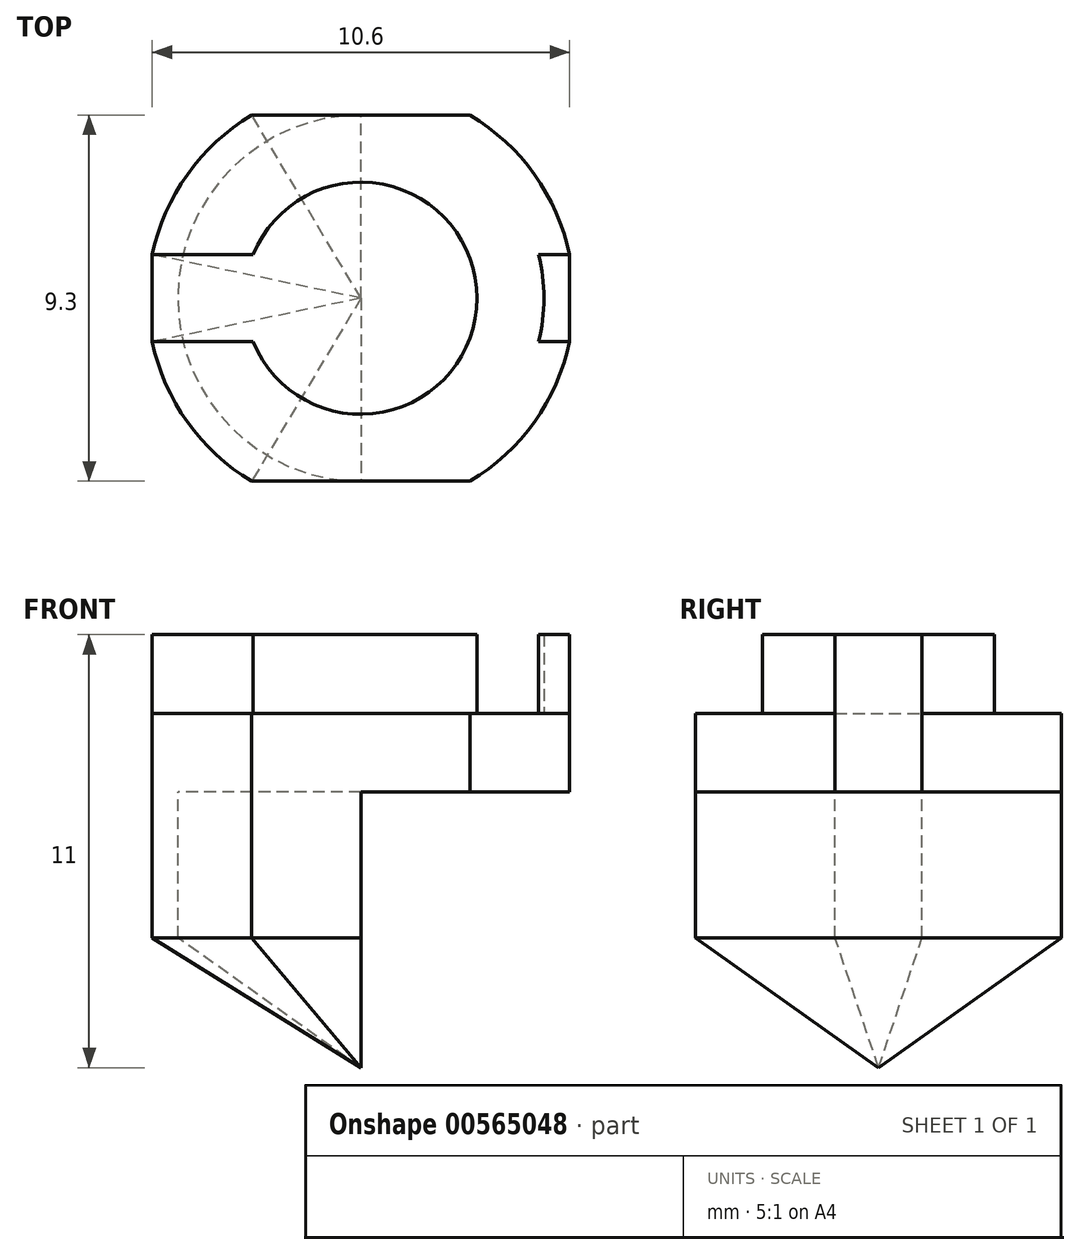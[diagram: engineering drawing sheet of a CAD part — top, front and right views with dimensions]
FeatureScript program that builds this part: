
annotation { "Feature Type Name" : "Feature", "Feature Type Description" : "" }
export const myFeature = defineFeature(function(context is Context, id is Id, definition is map)
    precondition{}
    {
        {
            var Q0;
            Q0=qCreatedBy(makeId("Top.planeOp"),FACE);
            var sketch = newSketch(context, id + "F0", { "sketchPlane" : qUnion([Q0])});
            skLineSegment(sketch, "E0.top", {"start": v(-2.77, 4.65) * mm, "end": v(0, 4.65) * mm});
            skArc(sketch, "E1", {"start": v(0, 2.95) * mm, "mid": v(-2.09, 2.09) * mm, "end": v(-2.95, 0) * mm});
            skLineSegment(sketch, "E2.bottom", {"start": v(-5.3, 1.1) * mm, "end": v(-2.74, 1.1) * mm});
            skPoint(sketch, "E2.middle", {"position": v(-2.95, 0) * mm});
            skArc(sketch, "E3", {"start": v(0, 4.65) * mm, "mid": v(-2.87, 3.66) * mm, "end": v(-4.52, 1.1) * mm});
            skArc(sketch, "E4.0", {"start": v(-2.77, 4.65) * mm, "mid": v(-4.4, 3.14) * mm, "end": v(-5.3, 1.1) * mm});
            skPoint(sketch, "E5", {"position": v(0, 2.95) * mm});
            skLineSegment(sketch, "E6.MirrorCS", {"start": v(2.77, 4.65) * mm, "end": v(0, 4.65) * mm});
            skArc(sketch, "E7.MirrorCS", {"start": v(0, 4.65) * mm, "mid": v(2.87, 3.66) * mm, "end": v(4.52, 1.1) * mm});
            skArc(sketch, "E8.MirrorCS", {"start": v(2.77, 4.65) * mm, "mid": v(4.4, 3.14) * mm, "end": v(5.3, 1.1) * mm});
            skArc(sketch, "E9.MirrorCS", {"start": v(0, 2.95) * mm, "mid": v(2.09, 2.09) * mm, "end": v(2.95, 0) * mm});
            skLineSegment(sketch, "E10.MirrorCS", {"start": v(5.3, 1.1) * mm, "end": v(2.74, 1.1) * mm});
            skArc(sketch, "E11.MirrorCS", {"start": v(0, -2.95) * mm, "mid": v(-2.09, -2.09) * mm, "end": v(-2.95, 0) * mm});
            skArc(sketch, "E12.MirrorCS", {"start": v(0, -2.95) * mm, "mid": v(2.09, -2.09) * mm, "end": v(2.95, 0) * mm});
            skLineSegment(sketch, "E13.MirrorCS", {"start": v(5.3, -1.1) * mm, "end": v(2.74, -1.1) * mm});
            skLineSegment(sketch, "E14.MirrorCS", {"start": v(-5.3, -1.1) * mm, "end": v(-2.74, -1.1) * mm});
            skArc(sketch, "E15.MirrorCS", {"start": v(0, -4.65) * mm, "mid": v(-2.87, -3.66) * mm, "end": v(-4.52, -1.1) * mm});
            skArc(sketch, "E16.MirrorCS", {"start": v(-2.77, -4.65) * mm, "mid": v(-4.4, -3.14) * mm, "end": v(-5.3, -1.1) * mm});
            skLineSegment(sketch, "E17.MirrorCS", {"start": v(-2.77, -4.65) * mm, "end": v(0, -4.65) * mm});
            skLineSegment(sketch, "E18.MirrorCS", {"start": v(2.77, -4.65) * mm, "end": v(0, -4.65) * mm});
            skArc(sketch, "E19.MirrorCS", {"start": v(2.77, -4.65) * mm, "mid": v(4.4, -3.14) * mm, "end": v(5.3, -1.1) * mm});
            skArc(sketch, "E20.MirrorCS", {"start": v(0, -4.65) * mm, "mid": v(2.87, -3.66) * mm, "end": v(4.52, -1.1) * mm});
            skLineSegment(sketch, "E21", {"start": v(-5.3, 1.1) * mm, "end": v(-5.3, -1.1) * mm});
            skLineSegment(sketch, "E22", {"start": v(5.3, 1.1) * mm, "end": v(5.3, -1.1) * mm});
            skCircle(sketch, "E23", {"center": v(0, 0) * mm, "radius": 4.65 * mm});
            skSolve(sketch);
        }
        {
            var Q0;
            {var subQ8=sQuery(id+"F0.wireOp",EDGE,"E21");Q0=makeQuery(id+"F0.imprint","IMPRINT",FACE,{"disambiguationData":[TD([[makeQuery(id+"F0.imprint","IMPRINT",EDGE,{"derivedFrom":subQ8}),1.0]])]});}
            var Q1;
            {var subQ0=sQuery(id+"F0.wireOp",EDGE,"E9.MirrorCS");var subQ1=sQuery(id+"F0.wireOp",EDGE,"E1");var subQ2=makeQuery(id+"F0.imprint","INTERSECT",VERTEX,{"derivedFrom":[subQ1,subQ0]});Q1=makeQuery(id+"F0.imprint","IMPRINT",FACE,{"disambiguationData":[TD([[makeQuery(id+"F0.imprint","IMPRINT",EDGE,{"disambiguationData":[TD([[subQ2,-1.0]])],"derivedFrom":subQ1}),1.0]])]});}
            var Q2;
            {var subQ8=sQuery(id+"F0.wireOp",EDGE,"E22");Q2=makeQuery(id+"F0.imprint","IMPRINT",FACE,{"disambiguationData":[TD([[makeQuery(id+"F0.imprint","IMPRINT",EDGE,{"derivedFrom":subQ8}),-1.0]])]});}
            var Q3;
            {var subQ0=sQuery(id+"F0.wireOp",EDGE,"E11.MirrorCS");var subQ1=sQuery(id+"F0.wireOp",EDGE,"E1");var subQ2=makeQuery(id+"F0.imprint","INTERSECT",VERTEX,{"derivedFrom":[subQ1,subQ0]});Q3=makeQuery(id+"F0.imprint","IMPRINT",FACE,{"disambiguationData":[TD([[makeQuery(id+"F0.imprint","IMPRINT",EDGE,{"disambiguationData":[TD([[subQ2,1.0]])],"derivedFrom":subQ1}),-1.0]])]});}
            var Q4;
            {var subQ1=sQuery(id+"F0.wireOp",EDGE,"E12.MirrorCS");var subQ5=sQuery(id+"F0.wireOp",EDGE,"E9.MirrorCS");var subQ6=makeQuery(id+"F0.imprint","INTERSECT",VERTEX,{"derivedFrom":[subQ5,subQ1]});Q4=makeQuery(id+"F0.imprint","IMPRINT",FACE,{"disambiguationData":[TD([[makeQuery(id+"F0.imprint","IMPRINT",EDGE,{"disambiguationData":[TD([[subQ6,1.0]])],"derivedFrom":subQ5}),1.0]])]});}
            extrude(context, id + "F1", {"entities" : qUnion([Q0, Q1, Q2, Q3, Q4]), "depth" : 2 * mm, "offsetDistance" : 25 * mm});
        }
        {
            var Q0;
            Q0=makeQuery(id+"F1.opExtrude","CAP_FACE",FACE,{"disambiguationData":[OSD([sQuery(id+"F0.wireOp",EDGE,"E1"),sQuery(id+"F0.wireOp",EDGE,"E2.bottom"),sQuery(id+"F0.wireOp",EDGE,"E9.MirrorCS"),sQuery(id+"F0.wireOp",EDGE,"E10.MirrorCS"),sQuery(id+"F0.wireOp",EDGE,"E11.MirrorCS"),sQuery(id+"F0.wireOp",EDGE,"E12.MirrorCS"),sQuery(id+"F0.wireOp",EDGE,"E13.MirrorCS"),sQuery(id+"F0.wireOp",EDGE,"E14.MirrorCS"),sQuery(id+"F0.wireOp",EDGE,"E21"),sQuery(id+"F0.wireOp",EDGE,"E22")])],"isStart":true});
            var sketch = newSketch(context, id + "F2", { "sketchPlane" : qUnion([Q0])});
            skLineSegment(sketch, "E24.0", {"start": v(-5.3, -1.1) * mm, "end": v(-5.3, 1.1) * mm});
            skArc(sketch, "E24.1", {"start": v(-2.77, -4.65) * mm, "mid": v(-4.4, -3.14) * mm, "end": v(-5.3, -1.1) * mm});
            skLineSegment(sketch, "E24.2", {"start": v(-2.77, -4.65) * mm, "end": v(0, -4.65) * mm});
            skLineSegment(sketch, "E24.3", {"start": v(2.77, -4.65) * mm, "end": v(0, -4.65) * mm});
            skArc(sketch, "E24.4", {"start": v(2.77, -4.65) * mm, "mid": v(4.4, -3.14) * mm, "end": v(5.3, -1.1) * mm});
            skLineSegment(sketch, "E24.5", {"start": v(5.3, -1.1) * mm, "end": v(5.3, 1.1) * mm});
            skArc(sketch, "E24.6", {"start": v(2.77, 4.65) * mm, "mid": v(4.4, 3.14) * mm, "end": v(5.3, 1.1) * mm});
            skLineSegment(sketch, "E24.7", {"start": v(2.77, 4.65) * mm, "end": v(0, 4.65) * mm});
            skLineSegment(sketch, "E24.8", {"start": v(-2.77, 4.65) * mm, "end": v(0, 4.65) * mm});
            skArc(sketch, "E24.9", {"start": v(-2.77, 4.65) * mm, "mid": v(-4.4, 3.14) * mm, "end": v(-5.3, 1.1) * mm});
            skPoint(sketch, "E24.10", {"position": v(1.39, 4.65) * mm});
            skPoint(sketch, "E24.11", {"position": v(-1.39, 4.65) * mm});
            skSolve(sketch);
        }
        {
            var Q0;
            Q0 = qSketchRegion(id + "F2", true);
            extrude(context, id + "F3", {"entities" : qUnion([Q0]), "operationType" : NewBodyOperationType.ADD, "depth" : 2 * mm, "offsetDistance" : 25 * mm});
        }
        {
            var Q0;
            Q0=makeQuery(id+"F3.opExtrude","CAP_FACE",FACE,{"disambiguationData":[OSD([sQuery(id+"F2.wireOp",EDGE,"E24.0"),sQuery(id+"F2.wireOp",EDGE,"E24.1"),sQuery(id+"F2.wireOp",EDGE,"E24.2"),sQuery(id+"F2.wireOp",EDGE,"E24.3"),sQuery(id+"F2.wireOp",EDGE,"E24.4"),sQuery(id+"F2.wireOp",EDGE,"E24.5"),sQuery(id+"F2.wireOp",EDGE,"E24.6"),sQuery(id+"F2.wireOp",EDGE,"E24.7"),sQuery(id+"F2.wireOp",EDGE,"E24.8"),sQuery(id+"F2.wireOp",EDGE,"E24.9")])],"isStart":false});
            var sketch = newSketch(context, id + "F4", { "sketchPlane" : qUnion([Q0])});
            skCircle(sketch, "E25.0", {"center": v(0, 0) * mm, "radius": 4.65 * mm});
            skSolve(sketch);
        }
        {
            var Q0;
            {var subQ0=sQuery(id+"F4.wireOp",EDGE,"E25.0");var subQ1=makeQuery(id+"F4.imprint","INTERSECT",VERTEX,{"derivedFrom":[makeQuery(id+"F3.opExtrude","CAP_EDGE",EDGE,{"disambiguationData":[OSD([sQuery(id+"F2.wireOp",EDGE,"E24.2"),sQuery(id+"F2.wireOp",EDGE,"E24.3")])],"isStart":false}),subQ0]});Q0=makeQuery(id+"F4.imprint","IMPRINT",FACE,{"disambiguationData":[TD([[makeQuery(id+"F4.imprint","IMPRINT",EDGE,{"disambiguationData":[TD([[subQ1,1.0]])],"derivedFrom":subQ0}),-1.0]])]});}
            extrude(context, id + "F5", {"entities" : qUnion([Q0]), "operationType" : NewBodyOperationType.ADD, "depth" : 3.7 * mm, "offsetDistance" : 25 * mm});
        }
        {
            var Q0;
            Q0=qCreatedBy(makeId("Right.planeOp"),FACE);
            var sketch = newSketch(context, id + "F6", { "sketchPlane" : qUnion([Q0])});
            skLineSegment(sketch, "E26.0", {"start": v(1.1, 2) * mm, "end": v(-1.1, 2) * mm});
            skPoint(sketch, "E27", {"position": v(0, -9) * mm});
            skSolve(sketch);
        }
        {
            var Q1;
            Q1=sQuery(id+"F6.wireOp",VERTEX,"E27");
            var Q2;
            Q2=makeQuery(id+"F5.opExtrude","CAP_FACE",FACE,{"disambiguationData":[OSD([sQuery(id+"F4.wireOp",EDGE,"E25.0")])],"isStart":false});
            loft(context, id + "F7", {"operationType" : NewBodyOperationType.ADD, "sheetProfilesArray" : [{ "sheetProfileEntities" : qUnion([Q1]) }, { "sheetProfileEntities" : qUnion([Q2]) }]});
        }
    });
